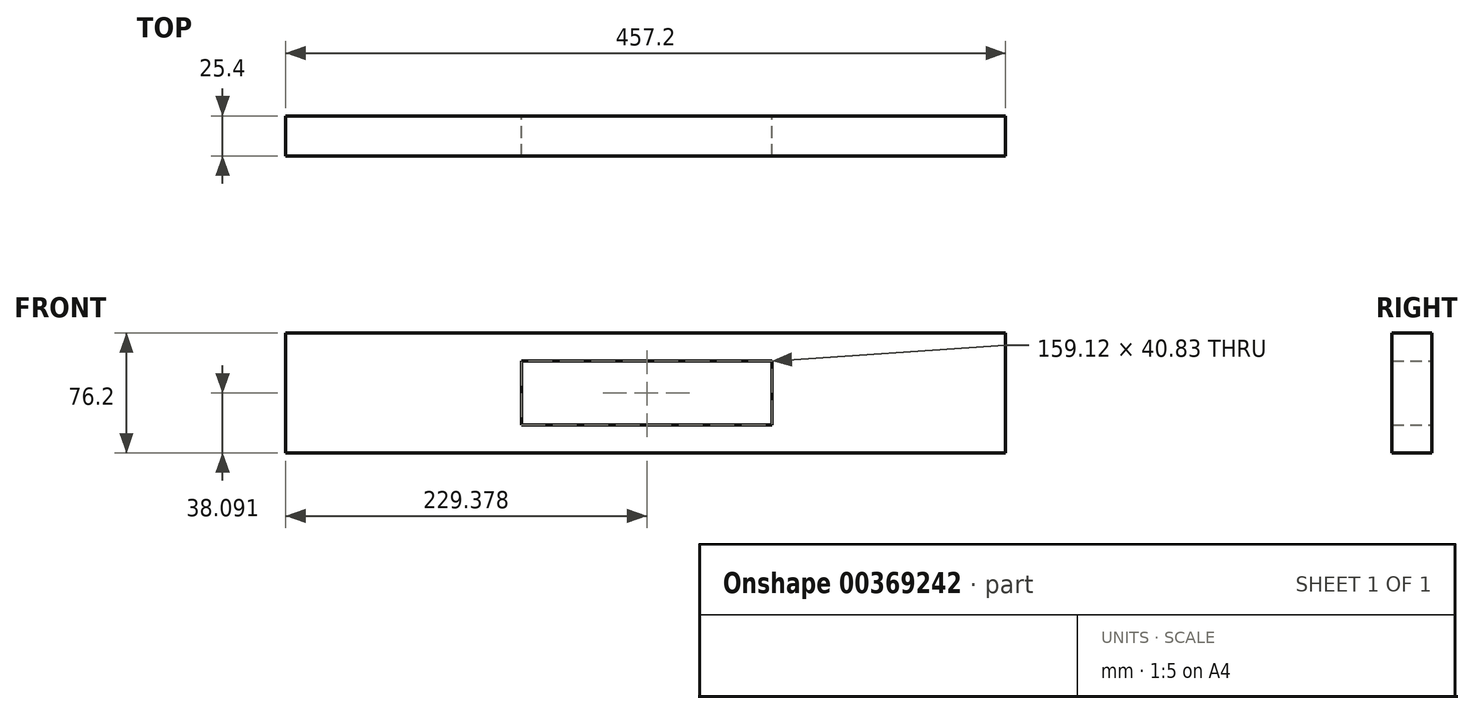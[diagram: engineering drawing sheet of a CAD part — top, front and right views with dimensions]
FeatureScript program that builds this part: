
annotation { "Feature Type Name" : "Feature", "Feature Type Description" : "" }
export const myFeature = defineFeature(function(context is Context, id is Id, definition is map)
    precondition{}
    {
        {
            var Q0;
            Q0=qCreatedBy(makeId("Front.planeOp"),FACE);
            var sketch = newSketch(context, id + "F0", { "sketchPlane" : qUnion([Q0])});
            skLineSegment(sketch, "E0.bottom", {"start": v(-262.53, 81.45) * mm, "end": v(194.67, 81.45) * mm});
            skLineSegment(sketch, "E0.top", {"start": v(-262.53, 5.25) * mm, "end": v(194.67, 5.25) * mm});
            skLineSegment(sketch, "E0.left", {"start": v(-262.53, 81.45) * mm, "end": v(-262.53, 5.25) * mm});
            skLineSegment(sketch, "E0.right", {"start": v(194.67, 81.45) * mm, "end": v(194.67, 5.25) * mm});
            skLineSegment(sketch, "E1.bottom", {"start": v(-112.71, 63.76) * mm, "end": v(46.4, 63.76) * mm});
            skLineSegment(sketch, "E1.top", {"start": v(-112.71, 22.93) * mm, "end": v(46.4, 22.93) * mm});
            skLineSegment(sketch, "E1.left", {"start": v(-112.71, 63.76) * mm, "end": v(-112.71, 22.93) * mm});
            skLineSegment(sketch, "E1.right", {"start": v(46.4, 63.76) * mm, "end": v(46.4, 22.93) * mm});
            skSolve(sketch);
        }
        {
            var Q0;
            Q0 = qSketchRegion(id + "F0", true);
            extrude(context, id + "F1", {"entities" : qUnion([Q0]), "depth" : 25.4 * mm});
        }
    });
